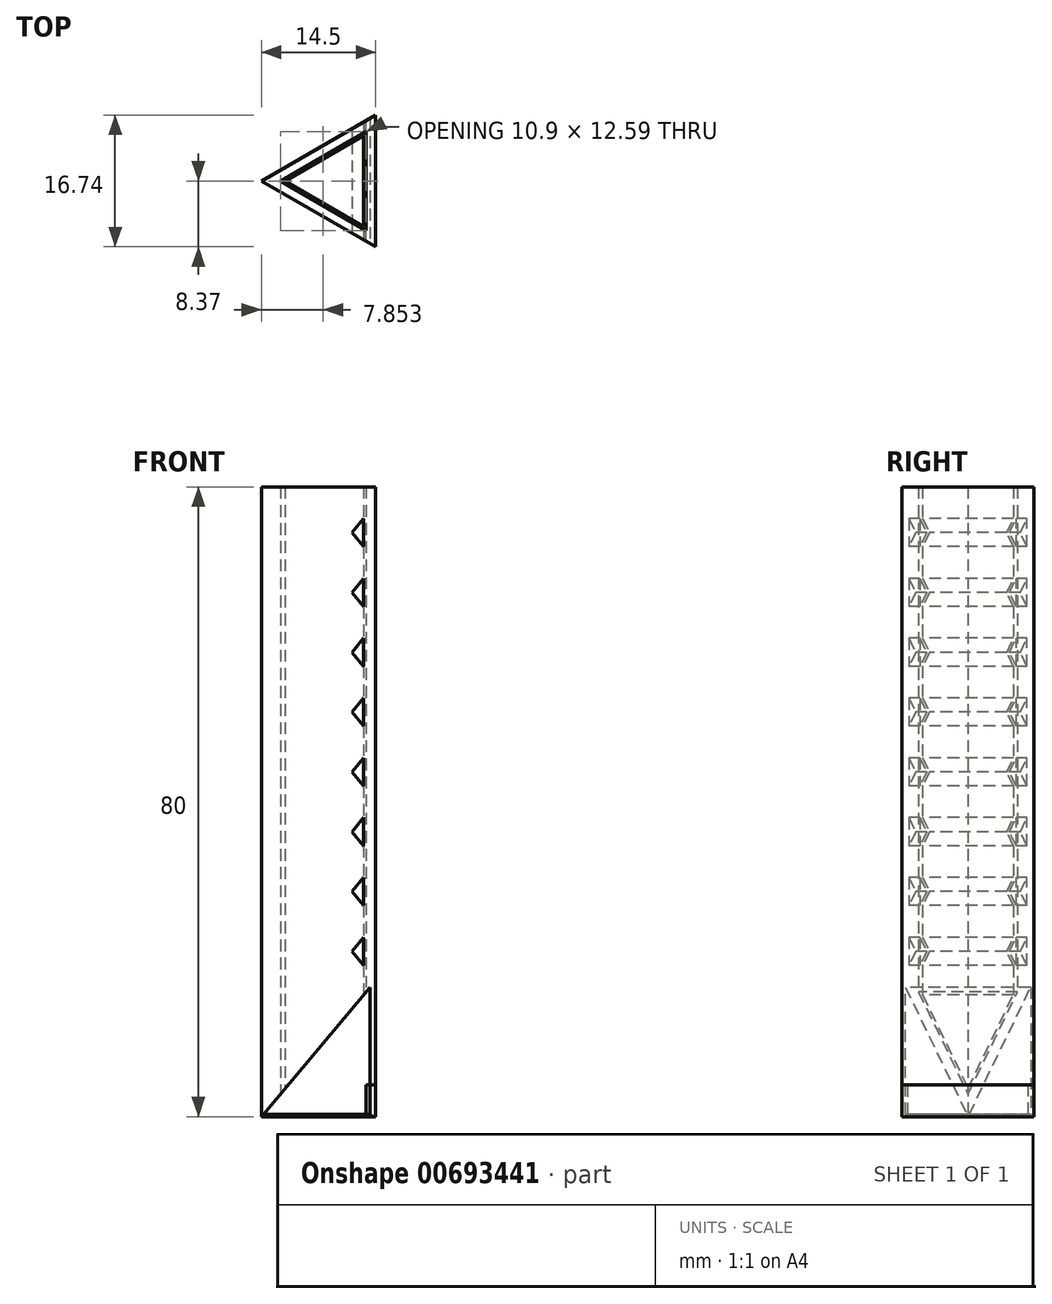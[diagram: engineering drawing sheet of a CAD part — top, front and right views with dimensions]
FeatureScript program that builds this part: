
annotation { "Feature Type Name" : "Feature", "Feature Type Description" : "" }
export const myFeature = defineFeature(function(context is Context, id is Id, definition is map)
    precondition{}
    {
        {
            var Q0;
            Q0=qCreatedBy(makeId("Top.planeOp"),FACE);
            var sketch = newSketch(context, id + "F0", { "sketchPlane" : qUnion([Q0])});
            skCircle(sketch, "E0.cCircle", {"center": v(0, 0) * mm, "radius": 3.33 * mm, "construction": true});
            skLineSegment(sketch, "E0.0", {"start": v(3.33, -5.77) * mm, "end": v(-6.67, 0) * mm});
            skLineSegment(sketch, "E0.1", {"start": v(-6.67, 0) * mm, "end": v(3.33, 5.77) * mm});
            skLineSegment(sketch, "E0.2", {"start": v(3.33, 5.77) * mm, "end": v(3.33, -5.77) * mm});
            skPoint(sketch, "E0.0.midPoint", {"position": v(-1.67, -2.89) * mm});
            skLineSegment(sketch, "E1.0", {"start": v(-7.27, 0) * mm, "end": v(3.63, 6.3) * mm});
            skLineSegment(sketch, "E1.1", {"start": v(3.63, -6.3) * mm, "end": v(-7.27, 0) * mm});
            skLineSegment(sketch, "E1.2", {"start": v(3.63, 6.3) * mm, "end": v(3.63, -6.3) * mm});
            skLineSegment(sketch, "E2.0", {"start": v(-9.67, 0) * mm, "end": v(4.83, 8.37) * mm});
            skLineSegment(sketch, "E2.1", {"start": v(4.83, -8.37) * mm, "end": v(-9.67, 0) * mm});
            skLineSegment(sketch, "E2.2", {"start": v(4.83, 8.37) * mm, "end": v(4.83, -8.37) * mm});
            skSolve(sketch);
        }
        {
            var Q0;
            Q0=makeQuery(id+"F0.imprint","IMPRINT",FACE,{"disambiguationData":[TD([[makeQuery(id+"F0.imprint","IMPRINT",EDGE,{"derivedFrom":sQuery(id+"F0.wireOp",EDGE,"E0.0")}),-1.0]])]});
            var Q1;
            Q1=makeQuery(id+"F0.imprint","IMPRINT",FACE,{"disambiguationData":[TD([[makeQuery(id+"F0.imprint","IMPRINT",EDGE,{"derivedFrom":sQuery(id+"F0.wireOp",EDGE,"E1.0")}),1.0]])]});
            extrude(context, id + "F1", {"entities" : qUnion([Q0, Q1]), "depth" : 80 * mm, "offsetDistance" : 25 * mm});
        }
        {
            var Q0;
            Q0=qCreatedBy(makeId("Front.planeOp"),FACE);
            var sketch = newSketch(context, id + "F2", { "sketchPlane" : qUnion([Q0])});
            skLineSegment(sketch, "E3.0", {"start": v(3.33, 80) * mm, "end": v(3.33, 0) * mm});
            skLineSegment(sketch, "E4", {"start": v(3.33, 75.98) * mm, "end": v(1.83, 74.19) * mm});
            skLineSegment(sketch, "E5", {"start": v(1.83, 74.19) * mm, "end": v(3.33, 72.4) * mm});
            skLineSegment(sketch, "E6", {"start": v(3.33, 75.98) * mm, "end": v(3.33, 80) * mm, "construction": true});
            skLineSegment(sketch, "E7.1.0.0", {"start": v(3.33, 68.38) * mm, "end": v(1.83, 66.6) * mm});
            skLineSegment(sketch, "E7.1.0.1", {"start": v(1.83, 66.6) * mm, "end": v(3.33, 64.8) * mm});
            skLineSegment(sketch, "E7.2.0.0", {"start": v(3.33, 60.78) * mm, "end": v(1.83, 59) * mm});
            skLineSegment(sketch, "E7.2.0.1", {"start": v(1.83, 59) * mm, "end": v(3.33, 57.2) * mm});
            skLineSegment(sketch, "E7.3.0.0", {"start": v(3.33, 53.18) * mm, "end": v(1.83, 51.4) * mm});
            skLineSegment(sketch, "E7.3.0.1", {"start": v(1.83, 51.4) * mm, "end": v(3.33, 49.6) * mm});
            skLineSegment(sketch, "E7.4.0.0", {"start": v(3.33, 45.59) * mm, "end": v(1.83, 43.8) * mm});
            skLineSegment(sketch, "E7.4.0.1", {"start": v(1.83, 43.8) * mm, "end": v(3.33, 42.01) * mm});
            skLineSegment(sketch, "E7.5.0.0", {"start": v(3.33, 37.99) * mm, "end": v(1.83, 36.2) * mm});
            skLineSegment(sketch, "E7.5.0.1", {"start": v(1.83, 36.2) * mm, "end": v(3.33, 34.41) * mm});
            skLineSegment(sketch, "E7.6.0.0", {"start": v(3.33, 30.4) * mm, "end": v(1.83, 28.6) * mm});
            skLineSegment(sketch, "E7.6.0.1", {"start": v(1.83, 28.6) * mm, "end": v(3.33, 26.82) * mm});
            skLineSegment(sketch, "E7.7.0.0", {"start": v(3.33, 22.8) * mm, "end": v(1.83, 21) * mm});
            skLineSegment(sketch, "E7.7.0.1", {"start": v(1.83, 21) * mm, "end": v(3.33, 19.22) * mm});
            skLineSegment(sketch, "E7.8.0.0", {"start": v(3.33, 15.2) * mm, "end": v(1.83, 13.4) * mm});
            skLineSegment(sketch, "E7.8.0.1", {"start": v(1.83, 13.4) * mm, "end": v(3.33, 11.62) * mm});
            skLineSegment(sketch, "E7.9.0.0", {"start": v(3.33, 7.6) * mm, "end": v(1.83, 5.81) * mm});
            skLineSegment(sketch, "E7.9.0.1", {"start": v(1.83, 5.81) * mm, "end": v(3.33, 4.02) * mm});
            skLineSegment(sketch, "E7.direction1", {"start": v(3.33, 72.4) * mm, "end": v(3.33, 64.8) * mm, "construction": true});
            skLineSegment(sketch, "E8", {"start": v(3.33, 4.02) * mm, "end": v(3.33, 0) * mm, "construction": true});
            skLineSegment(sketch, "E9", {"start": v(3.33, 68.38) * mm, "end": v(3.33, 72.4) * mm, "construction": true});
            skLineSegment(sketch, "E10", {"start": v(3.33, 49.6) * mm, "end": v(3.33, 45.59) * mm});
            skLineSegment(sketch, "E11", {"start": v(3.33, 57.2) * mm, "end": v(3.33, 53.18) * mm, "construction": true});
            skSolve(sketch);
        }
        {
            var Q0;
            {var subQ0=sQuery(id+"F2.wireOp",EDGE,"E4");Q0=makeQuery(id+"F2.imprint","IMPRINT",FACE,{"disambiguationData":[TD([[makeQuery(id+"F2.imprint","IMPRINT",EDGE,{"derivedFrom":subQ0}),1.0]])]});}
            var Q1;
            {var subQ0=sQuery(id+"F2.wireOp",EDGE,"E7.1.0.0");Q1=makeQuery(id+"F2.imprint","IMPRINT",FACE,{"disambiguationData":[TD([[makeQuery(id+"F2.imprint","IMPRINT",EDGE,{"derivedFrom":subQ0}),1.0]])]});}
            var Q2;
            {var subQ0=sQuery(id+"F2.wireOp",EDGE,"E7.2.0.0");Q2=makeQuery(id+"F2.imprint","IMPRINT",FACE,{"disambiguationData":[TD([[makeQuery(id+"F2.imprint","IMPRINT",EDGE,{"derivedFrom":subQ0}),1.0]])]});}
            var Q3;
            {var subQ0=sQuery(id+"F2.wireOp",EDGE,"E7.3.0.0");Q3=makeQuery(id+"F2.imprint","IMPRINT",FACE,{"disambiguationData":[TD([[makeQuery(id+"F2.imprint","IMPRINT",EDGE,{"derivedFrom":subQ0}),1.0]])]});}
            var Q4;
            {var subQ0=sQuery(id+"F2.wireOp",EDGE,"E7.4.0.0");Q4=makeQuery(id+"F2.imprint","IMPRINT",FACE,{"disambiguationData":[TD([[makeQuery(id+"F2.imprint","IMPRINT",EDGE,{"derivedFrom":subQ0}),1.0]])]});}
            var Q5;
            {var subQ0=sQuery(id+"F2.wireOp",EDGE,"E7.5.0.0");Q5=makeQuery(id+"F2.imprint","IMPRINT",FACE,{"disambiguationData":[TD([[makeQuery(id+"F2.imprint","IMPRINT",EDGE,{"derivedFrom":subQ0}),1.0]])]});}
            var Q6;
            {var subQ0=sQuery(id+"F2.wireOp",EDGE,"E7.6.0.0");Q6=makeQuery(id+"F2.imprint","IMPRINT",FACE,{"disambiguationData":[TD([[makeQuery(id+"F2.imprint","IMPRINT",EDGE,{"derivedFrom":subQ0}),1.0]])]});}
            var Q7;
            {var subQ0=sQuery(id+"F2.wireOp",EDGE,"E7.7.0.0");Q7=makeQuery(id+"F2.imprint","IMPRINT",FACE,{"disambiguationData":[TD([[makeQuery(id+"F2.imprint","IMPRINT",EDGE,{"derivedFrom":subQ0}),1.0]])]});}
            var Q8;
            {var subQ0=sQuery(id+"F2.wireOp",EDGE,"E7.8.0.0");Q8=makeQuery(id+"F2.imprint","IMPRINT",FACE,{"disambiguationData":[TD([[makeQuery(id+"F2.imprint","IMPRINT",EDGE,{"derivedFrom":subQ0}),1.0]])]});}
            var Q9;
            {var subQ0=sQuery(id+"F2.wireOp",EDGE,"E7.9.0.0");Q9=makeQuery(id+"F2.imprint","IMPRINT",FACE,{"disambiguationData":[TD([[makeQuery(id+"F2.imprint","IMPRINT",EDGE,{"derivedFrom":subQ0}),1.0]])]});}
            extrude(context, id + "F3", {"entities" : qUnion([Q0, Q1, Q2, Q3, Q4, Q5, Q6, Q7, Q8, Q9]), "operationType" : NewBodyOperationType.REMOVE, "endBound" : BoundingType.SYMMETRIC, "oppositeDirection" : true, "depth" : 25 * mm, "offsetDistance" : 25 * mm});
        }
        {
            var Q0;
            Q0=qCreatedBy(makeId("Front.planeOp"),FACE);
            var sketch = newSketch(context, id + "F4", { "sketchPlane" : qUnion([Q0])});
            skLineSegment(sketch, "E12", {"start": v(4.51, 16.9) * mm, "end": v(-9.41, 0.3) * mm});
            skLineSegment(sketch, "E13", {"start": v(-9.41, 0.3) * mm, "end": v(4.13, 0.3) * mm});
            skLineSegment(sketch, "E14", {"start": v(4.13, 0.3) * mm, "end": v(4.13, 16.9) * mm});
            skLineSegment(sketch, "E15", {"start": v(4.13, 16.9) * mm, "end": v(4.51, 16.9) * mm});
            skSolve(sketch);
        }
        {
            var Q0;
            Q0=makeQuery(id+"F4.imprint","IMPRINT",FACE,{"disambiguationData":[TD([[makeQuery(id+"F4.imprint","IMPRINT",EDGE,{"derivedFrom":sQuery(id+"F4.wireOp",EDGE,"E12")}),1.0]])]});
            extrude(context, id + "F5", {"entities" : qUnion([Q0]), "operationType" : NewBodyOperationType.REMOVE, "endBound" : BoundingType.SYMMETRIC, "oppositeDirection" : true, "depth" : 25 * mm, "offsetDistance" : 25 * mm});
        }
        {
            var Q0;
            Q0=qCreatedBy(makeId("Front.planeOp"),FACE);
            var sketch = newSketch(context, id + "F6", { "sketchPlane" : qUnion([Q0])});
            skLineSegment(sketch, "E16.0", {"start": v(3.63, 0.3) * mm, "end": v(3.63, 0.3) * mm});
            skLineSegment(sketch, "E17", {"start": v(3.63, 7.96) * mm, "end": v(3.63, 0.3) * mm});
            skLineSegment(sketch, "E18.0", {"start": v(4.83, 80) * mm, "end": v(4.83, 0) * mm});
            skLineSegment(sketch, "E19.0", {"start": v(3.63, 7.96) * mm, "end": v(1.83, 5.81) * mm});
            skLineSegment(sketch, "E19.1", {"start": v(1.83, 5.81) * mm, "end": v(3.33, 4.02) * mm});
            skLineSegment(sketch, "E20", {"start": v(4.83, 4.02) * mm, "end": v(4.83, 0) * mm});
            skLineSegment(sketch, "E21", {"start": v(4.83, 4.02) * mm, "end": v(3.33, 4.02) * mm});
            skLineSegment(sketch, "E22", {"start": v(4.83, 0) * mm, "end": v(3.63, 0.3) * mm});
            skSolve(sketch);
        }
        {
            var Q0;
            Q0=makeQuery(id+"F6.imprint","IMPRINT",FACE,{"disambiguationData":[TD([[makeQuery(id+"F6.imprint","IMPRINT",EDGE,{"derivedFrom":sQuery(id+"F6.wireOp",EDGE,"E17")}),1.0]])]});
            var Q1;
            Q1=makeQuery(id+"F1.opExtrude","SWEPT_FACE",FACE,{"disambiguationData":[OSD([sQuery(id+"F0.wireOp",EDGE,"E2.1")])]});
            var Q2;
            Q2=makeQuery(id+"F1.opExtrude","SWEPT_FACE",FACE,{"disambiguationData":[OSD([sQuery(id+"F0.wireOp",EDGE,"E2.0")])]});
            extrude(context, id + "F7", {"entities" : qUnion([Q0]), "endBound" : BoundingType.UP_TO_SURFACE, "depth" : 25 * mm, "endBoundEntityFace" : qUnion([Q1]), "offsetDistance" : 25 * mm, "hasSecondDirection" : true, "secondDirectionBound" : SecondDirectionBoundingType.UP_TO_SURFACE, "secondDirectionOppositeDirection" : true, "secondDirectionDepth" : 25 * mm, "secondDirectionBoundEntityFace" : qUnion([Q2])});
        }
    });
